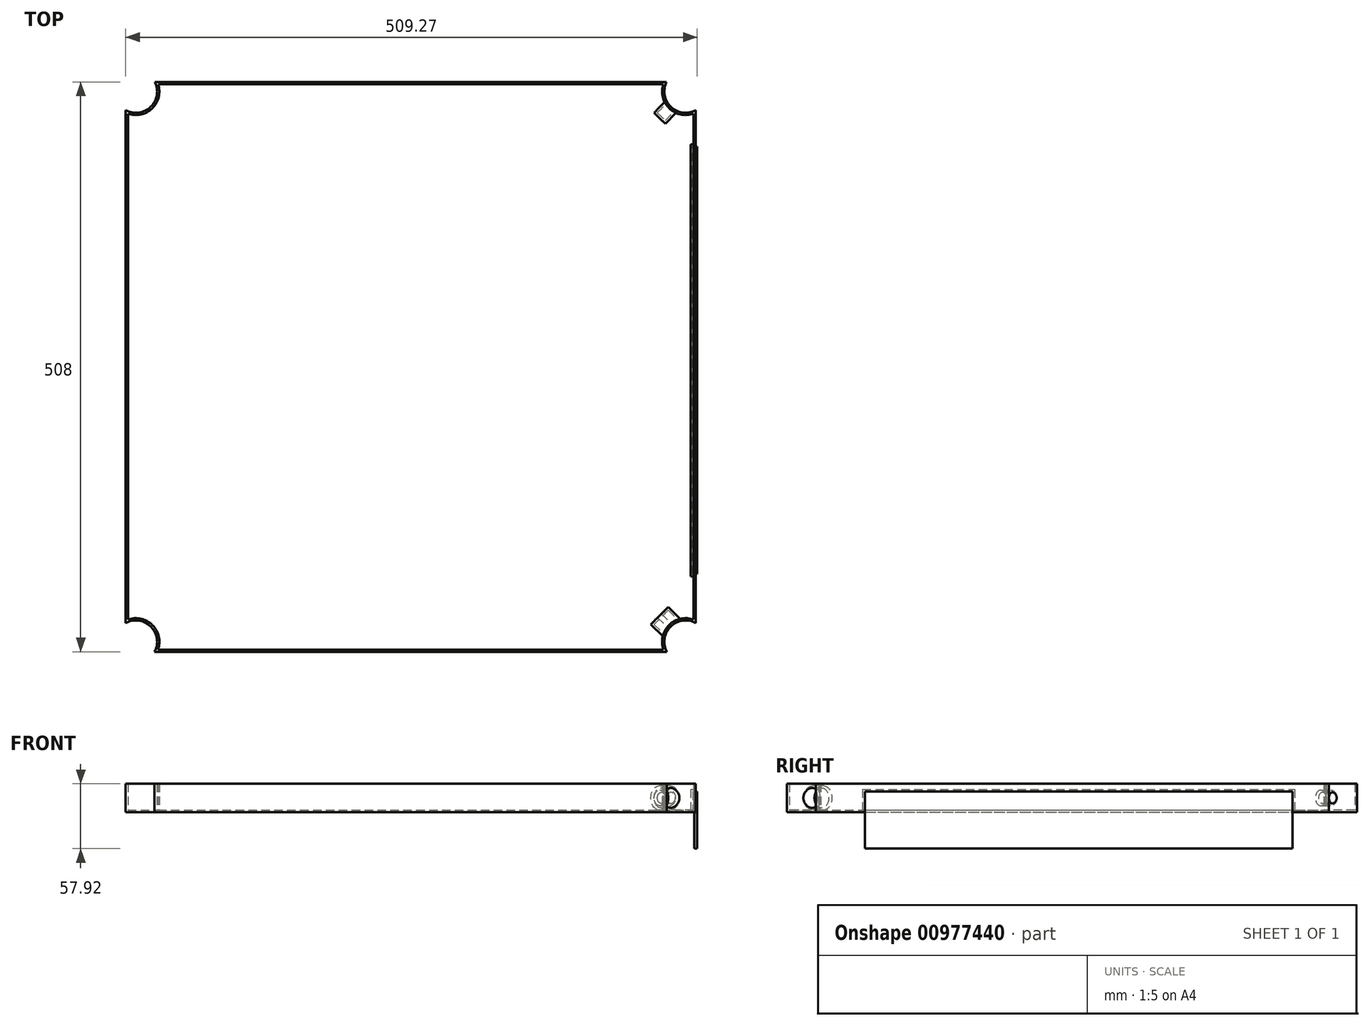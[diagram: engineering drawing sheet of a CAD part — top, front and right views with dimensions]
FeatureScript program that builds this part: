
annotation { "Feature Type Name" : "Feature", "Feature Type Description" : "" }
export const myFeature = defineFeature(function(context is Context, id is Id, definition is map)
    precondition{}
    {
        {
            var Q0;
            Q0=qCreatedBy(makeId("Top.planeOp"),FACE);
            var sketch = newSketch(context, id + "F0", { "sketchPlane" : qUnion([Q0])});
            skLineSegment(sketch, "E0.bottom", {"start": v(0, 0) * mm, "end": v(508, 0) * mm});
            skLineSegment(sketch, "E0.top", {"start": v(0, 508) * mm, "end": v(508, 508) * mm});
            skLineSegment(sketch, "E0.left", {"start": v(0, 0) * mm, "end": v(0, 508) * mm});
            skLineSegment(sketch, "E0.right", {"start": v(508, 0) * mm, "end": v(508, 508) * mm});
            skSolve(sketch);
        }
        {
            var Q0;
            Q0=makeQuery(id+"F0.imprint","IMPRINT",FACE,{"disambiguationData":[TD([[makeQuery(id+"F0.imprint","IMPRINT",EDGE,{"derivedFrom":sQuery(id+"F0.wireOp",EDGE,"E0.bottom")}),1.0]])]});
            extrude(context, id + "F1", {"entities" : qUnion([Q0]), "depth" : 25.4 * mm, "offsetDistance" : 25.4 * mm});
        }
        {
            var Q0;
            Q0=makeQuery(id+"F1.opExtrude","CAP_FACE",FACE,{"disambiguationData":[OSD([sQuery(id+"F0.wireOp",EDGE,"E0.bottom"),sQuery(id+"F0.wireOp",EDGE,"E0.top"),sQuery(id+"F0.wireOp",EDGE,"E0.left"),sQuery(id+"F0.wireOp",EDGE,"E0.right")])],"isStart":true});
            var sketch = newSketch(context, id + "F2", { "sketchPlane" : qUnion([Q0])});
            skLineSegment(sketch, "E1", {"start": v(0, 0) * mm, "end": v(0, 0) * mm});
            skLineSegment(sketch, "E2", {"start": v(0, 0) * mm, "end": v(508, 0) * mm, "construction": true});
            skLineSegment(sketch, "E3", {"start": v(508, 0) * mm, "end": v(254, 0) * mm, "construction": true});
            skLineSegment(sketch, "E4", {"start": v(254, 0) * mm, "end": v(254, -508.58) * mm, "construction": true});
            skLineSegment(sketch, "E5", {"start": v(254, -254.29) * mm, "end": v(508, -254.29) * mm, "construction": true});
            skLineSegment(sketch, "E6", {"start": v(0, 0) * mm, "end": v(8.98, -8.98) * mm, "construction": true});
            skCircle(sketch, "E7", {"center": v(8.98, -8.98) * mm, "radius": 19.05 * mm});
            skCircle(sketch, "E8.MirrorC", {"center": v(499.02, -8.98) * mm, "radius": 19.05 * mm});
            skCircle(sketch, "E9.MirrorC", {"center": v(8.98, -499.6) * mm, "radius": 19.05 * mm});
            skCircle(sketch, "E10.MirrorC", {"center": v(499.02, -499.6) * mm, "radius": 19.05 * mm});
            skSolve(sketch);
        }
        {
            var Q0;
            Q0 = qSketchRegion(id + "F2", true);
            extrude(context, id + "F3", {"entities" : qUnion([Q0]), "operationType" : NewBodyOperationType.REMOVE, "oppositeDirection" : true, "depth" : 25.4 * mm, "offsetDistance" : 25.4 * mm});
        }
        {
            var Q0;
            Q0=makeQuery(id+"F3.boolean.opBoolean","INTERSECT",EDGE,{"derivedFrom":[makeQuery(id+"F1.opExtrude","SWEPT_FACE",FACE,{"disambiguationData":[OSD([sQuery(id+"F0.wireOp",EDGE,"E0.right")])]}),makeQuery(id+"F3.opExtrude","SWEPT_FACE",FACE,{"disambiguationData":[OSD([sQuery(id+"F2.wireOp",EDGE,"E10.MirrorC")])]})]});
            var Q1;
            Q1=makeQuery(id+"F3.boolean.opBoolean","INTERSECT",EDGE,{"derivedFrom":[makeQuery(id+"F1.opExtrude","SWEPT_FACE",FACE,{"disambiguationData":[OSD([sQuery(id+"F0.wireOp",EDGE,"E0.top")])]}),makeQuery(id+"F3.opExtrude","SWEPT_FACE",FACE,{"disambiguationData":[OSD([sQuery(id+"F2.wireOp",EDGE,"E10.MirrorC")])]})]});
            cPlane(context, id + "F4", {"entities" : qUnion([Q0, Q1]), "cplaneType" : CPlaneType.LINE_ANGLE, "offset" : 25.4 * mm, "angle" : 0 * degree, "width" : 152.4 * mm, "height" : 152.4 * mm});
        }
        {
            var Q0;
            Q0=qCreatedBy(id+"F4.planeOp",FACE);
            var sketch = newSketch(context, id + "F5", { "sketchPlane" : qUnion([Q0])});
            skLineSegment(sketch, "E11", {"start": v(-29.72, 25.4) * mm, "end": v(-29.72, 0) * mm, "construction": true});
            skLineSegment(sketch, "E12", {"start": v(-29.72, 0) * mm, "end": v(6.54, 0) * mm, "construction": true});
            skLineSegment(sketch, "E13", {"start": v(6.54, 0) * mm, "end": v(6.54, 25.4) * mm, "construction": true});
            skLineSegment(sketch, "E14", {"start": v(6.54, 25.4) * mm, "end": v(-29.72, 25.4) * mm, "construction": true});
            skLineSegment(sketch, "E15", {"start": v(-11.59, 25.4) * mm, "end": v(-11.59, 0) * mm, "construction": true});
            skCircle(sketch, "E16", {"center": v(-11.59, 12.7) * mm, "radius": 4.97 * mm});
            skSolve(sketch);
        }
        {
            var Q0;
            Q0 = qSketchRegion(id + "F5", true);
            extrude(context, id + "F6", {"entities" : qUnion([Q0]), "operationType" : NewBodyOperationType.REMOVE, "oppositeDirection" : true, "depth" : 25.4 * mm, "offsetDistance" : 25.4 * mm});
        }
        {
            var Q0;
            Q0=makeQuery(id+"F1.opExtrude","SWEPT_FACE",FACE,{"disambiguationData":[OSD([sQuery(id+"F0.wireOp",EDGE,"E0.right")])]});
            var sketch = newSketch(context, id + "F7", { "sketchPlane" : qUnion([Q0])});
            skLineSegment(sketch, "E17", {"start": v(482.8, 25.4) * mm, "end": v(482.8, 12.7) * mm, "construction": true});
            skLineSegment(sketch, "E18", {"start": v(25.78, 12.7) * mm, "end": v(25.78, 25.4) * mm, "construction": true});
            skLineSegment(sketch, "E19", {"start": v(254.29, 25.4) * mm, "end": v(254.29, 0) * mm, "construction": true});
            skLineSegment(sketch, "E20.bottom", {"start": v(69.38, 13.2) * mm, "end": v(450.38, 13.2) * mm, "construction": true});
            skLineSegment(sketch, "E21", {"start": v(69.38, 13.2) * mm, "end": v(69.38, 18.28) * mm});
            skLineSegment(sketch, "E22", {"start": v(450.38, 13.2) * mm, "end": v(450.38, 18.28) * mm});
            skLineSegment(sketch, "E23.bottom", {"start": v(69.38, 18.28) * mm, "end": v(450.38, 18.28) * mm});
            skLineSegment(sketch, "E23.top", {"start": v(69.38, -32.52) * mm, "end": v(450.38, -32.52) * mm});
            skLineSegment(sketch, "E23.left", {"start": v(69.38, 18.28) * mm, "end": v(69.38, -32.52) * mm});
            skLineSegment(sketch, "E23.right", {"start": v(450.38, 18.28) * mm, "end": v(450.38, -32.52) * mm});
            skSolve(sketch);
        }
        {
            var Q0;
            Q0 = qSketchRegion(id + "F7", true);
            extrude(context, id + "F8", {"entities" : qUnion([Q0]), "operationType" : NewBodyOperationType.REMOVE, "oppositeDirection" : true, "depth" : 2.54 * mm, "offsetDistance" : 25.4 * mm});
        }
        {
            var Q0;
            Q0 = qSketchRegion(id + "F7", true);
            extrude(context, id + "F9", {"entities" : qUnion([Q0]), "endBound" : BoundingType.SYMMETRIC, "depth" : 2.54 * mm, "offsetDistance" : 25.4 * mm});
        }
        {
            var Q0;
            Q0=makeQuery(id+"F3.boolean.opBoolean","INTERSECT",EDGE,{"derivedFrom":[makeQuery(id+"F1.opExtrude","SWEPT_FACE",FACE,{"disambiguationData":[OSD([sQuery(id+"F0.wireOp",EDGE,"E0.right")])]}),makeQuery(id+"F3.opExtrude","SWEPT_FACE",FACE,{"disambiguationData":[OSD([sQuery(id+"F2.wireOp",EDGE,"E8.MirrorC")])]})]});
            var Q1;
            Q1=makeQuery(id+"F3.boolean.opBoolean","INTERSECT",EDGE,{"derivedFrom":[makeQuery(id+"F1.opExtrude","SWEPT_FACE",FACE,{"disambiguationData":[OSD([sQuery(id+"F0.wireOp",EDGE,"E0.bottom")])]}),makeQuery(id+"F3.opExtrude","SWEPT_FACE",FACE,{"disambiguationData":[OSD([sQuery(id+"F2.wireOp",EDGE,"E8.MirrorC")])]})]});
            cPlane(context, id + "F10", {"entities" : qUnion([Q0, Q1]), "cplaneType" : CPlaneType.LINE_ANGLE, "offset" : 25.4 * mm, "angle" : 0 * degree, "width" : 152.4 * mm, "height" : 152.4 * mm});
        }
        {
            var Q0;
            Q0=qCreatedBy(id+"F10.planeOp",FACE);
            var sketch = newSketch(context, id + "F11", { "sketchPlane" : qUnion([Q0])});
            skLineSegment(sketch, "E24", {"start": v(-377.44, 25.4) * mm, "end": v(-377.44, 0) * mm, "construction": true});
            skLineSegment(sketch, "E25", {"start": v(-377.44, 0) * mm, "end": v(-340.98, 0) * mm, "construction": true});
            skLineSegment(sketch, "E26", {"start": v(-340.98, 0) * mm, "end": v(-340.98, 25.4) * mm, "construction": true});
            skLineSegment(sketch, "E27", {"start": v(-340.98, 25.4) * mm, "end": v(-377.44, 25.4) * mm, "construction": true});
            skLineSegment(sketch, "E28", {"start": v(-359.21, 25.4) * mm, "end": v(-359.21, 0) * mm, "construction": true});
            skCircle(sketch, "E29", {"center": v(-359.21, 12.7) * mm, "radius": 8.96 * mm});
            skSolve(sketch);
        }
        {
            var Q0;
            Q0 = qSketchRegion(id + "F11", true);
            extrude(context, id + "F12", {"entities" : qUnion([Q0]), "operationType" : NewBodyOperationType.REMOVE, "depth" : 25.4 * mm, "offsetDistance" : 25.4 * mm});
        }
        {
            var Q0;
            Q0=makeQuery(id+"F1.opExtrude","SWEPT_FACE",FACE,{"disambiguationData":[OSD([sQuery(id+"F0.wireOp",EDGE,"E0.right")])]});
            var Q1;
            Q1=makeQuery(id+"F1.opExtrude","SWEPT_FACE",FACE,{"disambiguationData":[OSD([sQuery(id+"F0.wireOp",EDGE,"E0.left")])]});
            cPlane(context, id + "F13", {"entities" : qUnion([Q0, Q1]), "cplaneType" : CPlaneType.MID_PLANE, "offset" : 25.4 * mm, "width" : 152.4 * mm, "height" : 152.4 * mm});
        }
        {
            var Q0;
            Q0=makeQuery(id+"F1.opExtrude","CAP_FACE",FACE,{"disambiguationData":[OSD([sQuery(id+"F0.wireOp",EDGE,"E0.bottom"),sQuery(id+"F0.wireOp",EDGE,"E0.top"),sQuery(id+"F0.wireOp",EDGE,"E0.left"),sQuery(id+"F0.wireOp",EDGE,"E0.right")])],"isStart":false});
            shell(context, id + "F14", {"entities" : qUnion([Q0]), "thickness" : 2 * mm});
        }
    });
